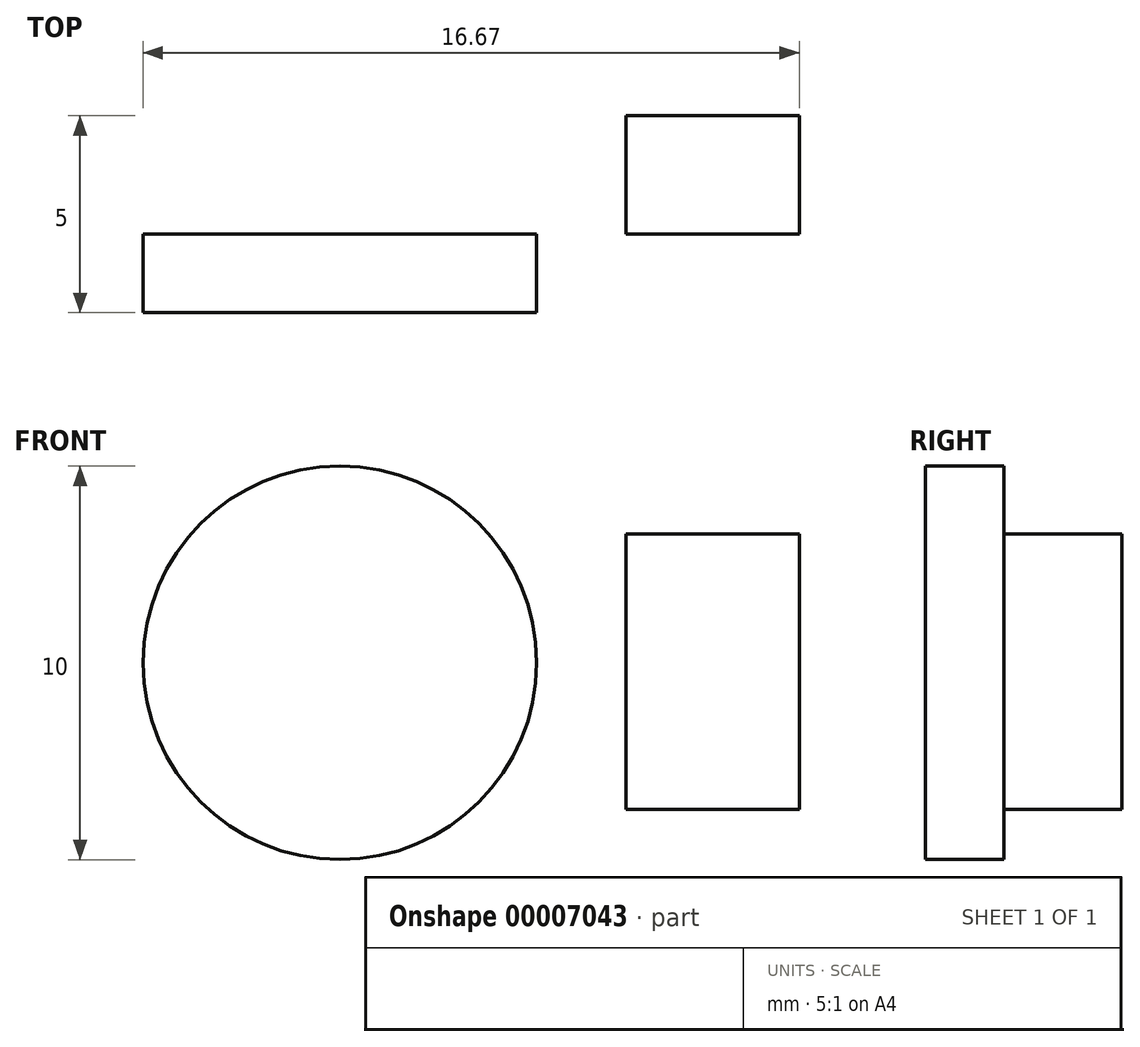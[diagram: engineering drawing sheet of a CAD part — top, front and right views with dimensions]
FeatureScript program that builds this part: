
annotation { "Feature Type Name" : "Feature", "Feature Type Description" : "" }
export const myFeature = defineFeature(function(context is Context, id is Id, definition is map)
    precondition{}
    {
        {
            var Q0;
            Q0=qCreatedBy(makeId("Top.planeOp"),FACE);
            var sketch = newSketch(context, id + "F0", { "sketchPlane" : qUnion([Q0])});
            skLineSegment(sketch, "E0.bottom", {"start": v(0, 0) * mm, "end": v(4.4, 0) * mm});
            skLineSegment(sketch, "E0.top", {"start": v(0, 3) * mm, "end": v(4.4, 3) * mm});
            skLineSegment(sketch, "E0.left", {"start": v(0, 0) * mm, "end": v(0, 3) * mm});
            skLineSegment(sketch, "E0.right", {"start": v(4.4, 0) * mm, "end": v(4.4, 3) * mm});
            skSolve(sketch);
        }
        {
            var Q0;
            Q0 = qSketchRegion(id + "F0", true);
            extrude(context, id + "F1", {"entities" : qUnion([Q0]), "depth" : 7 * mm});
        }
        {
            var Q0;
            Q0=qCreatedBy(makeId("Front.planeOp"),FACE);
            var sketch = newSketch(context, id + "F2", { "sketchPlane" : qUnion([Q0])});
            skCircle(sketch, "E1", {"center": v(-7.27, 3.72) * mm, "radius": 5 * mm});
            skSolve(sketch);
        }
        {
            var Q0;
            Q0 = qSketchRegion(id + "F2", true);
            extrude(context, id + "F3", {"entities" : qUnion([Q0]), "depth" : 2 * mm});
        }
    });
